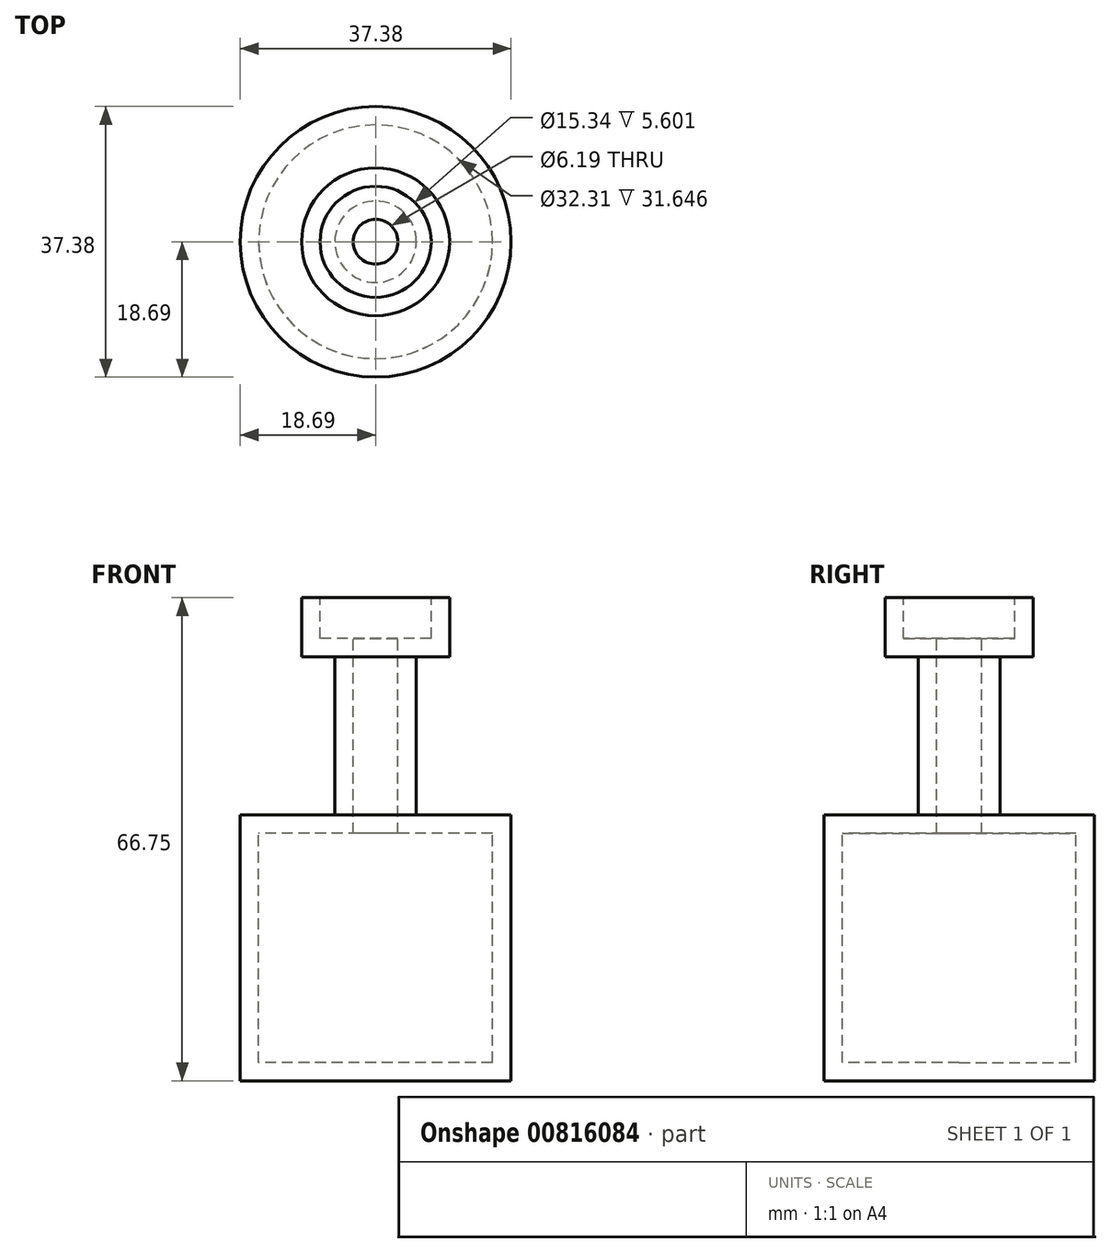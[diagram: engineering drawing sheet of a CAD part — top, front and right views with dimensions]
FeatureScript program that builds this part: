
annotation { "Feature Type Name" : "Feature", "Feature Type Description" : "" }
export const myFeature = defineFeature(function(context is Context, id is Id, definition is map)
    precondition{}
    {
        {
            var Q0;
            Q0=qCreatedBy(makeId("Front.planeOp"),FACE);
            var sketch = newSketch(context, id + "F0", { "sketchPlane" : qUnion([Q0])});
            skLineSegment(sketch, "E0", {"start": v(0, 66.75) * mm, "end": v(-10.21, 66.75) * mm});
            skLineSegment(sketch, "E1", {"start": v(-10.21, 66.75) * mm, "end": v(-10.21, 58.6) * mm});
            skLineSegment(sketch, "E2", {"start": v(-10.21, 58.6) * mm, "end": v(-5.63, 58.6) * mm});
            skLineSegment(sketch, "E3", {"start": v(-5.63, 58.6) * mm, "end": v(-5.63, 36.73) * mm});
            skLineSegment(sketch, "E4", {"start": v(-5.63, 36.73) * mm, "end": v(-18.7, 36.73) * mm});
            skLineSegment(sketch, "E5", {"start": v(-18.7, 36.73) * mm, "end": v(-18.7, 0) * mm});
            skLineSegment(sketch, "E6", {"start": v(-18.7, 0) * mm, "end": v(0, 0) * mm});
            skLineSegment(sketch, "E7", {"start": v(0, 66.75) * mm, "end": v(0, 0) * mm});
            skSolve(sketch);
        }
        {
            var Q0;
            Q0=makeQuery(id+"F0.imprint","IMPRINT",FACE,{"disambiguationData":[TD([[makeQuery(id+"F0.imprint","IMPRINT",EDGE,{"derivedFrom":sQuery(id+"F0.wireOp",EDGE,"E0")}),1.0]])]});
            var Q1;
            Q1=sQuery(id+"F0.wireOp",EDGE,"E7");
            revolve(context, id + "F1", {"surfaceOperationType" : NewSurfaceOperationType.NEW, "entities" : qUnion([Q0]), "axis" : qUnion([Q1]), "revolveType" : RevolveType.FULL});
        }
        {
            var Q0;
            Q0=makeQuery(id+"F1.opRevolve","SWEPT_FACE",FACE,{"disambiguationData":[OSD([sQuery(id+"F0.wireOp",EDGE,"E0")])]});
            shell(context, id + "F2", {"entities" : qUnion([Q0]), "thickness" : 2.54 * mm});
        }
    });
